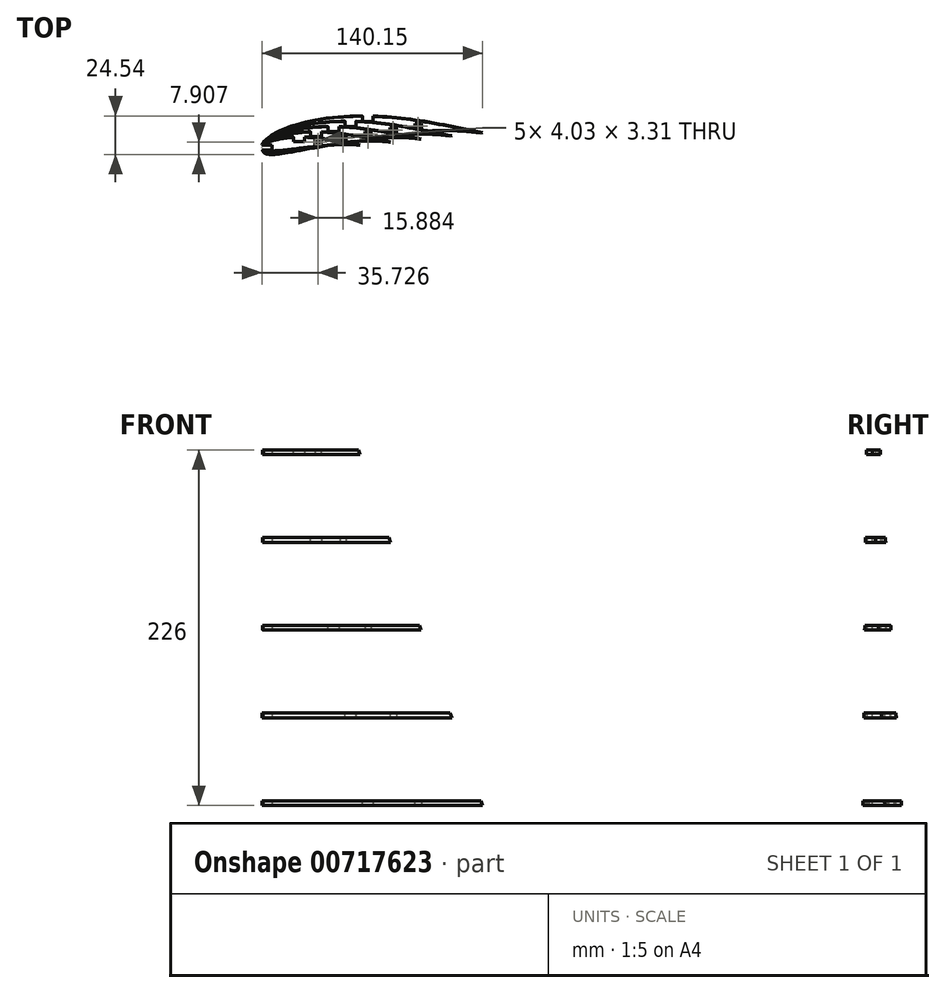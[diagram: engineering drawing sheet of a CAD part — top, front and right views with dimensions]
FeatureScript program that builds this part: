
annotation { "Feature Type Name" : "Feature", "Feature Type Description" : "" }
export const myFeature = defineFeature(function(context is Context, id is Id, definition is map)
    precondition{}
    {
        {
            var Q0;
            Q0=qCreatedBy(makeId("Top.planeOp"),FACE);
            var sketch = newSketch(context, id + "F0", { "sketchPlane" : qUnion([Q0])});
            skLineSegment(sketch, "E0", {"start": v(-0.42, 1.1) * mm, "end": v(1.04, 2.87) * mm});
            skLineSegment(sketch, "E1", {"start": v(1.04, 2.87) * mm, "end": v(2.54, 4.58) * mm});
            skLineSegment(sketch, "E2", {"start": v(2.54, 4.58) * mm, "end": v(4.15, 6.16) * mm});
            skLineSegment(sketch, "E3", {"start": v(4.15, 6.16) * mm, "end": v(4.64, 6.58) * mm});
            skLineSegment(sketch, "E4", {"start": v(4.64, 6.58) * mm, "end": v(5.9, 7.56) * mm});
            skLineSegment(sketch, "E5", {"start": v(5.9, 7.56) * mm, "end": v(7.8, 8.78) * mm});
            skLineSegment(sketch, "E6", {"start": v(7.8, 8.78) * mm, "end": v(9.8, 9.86) * mm});
            skLineSegment(sketch, "E7", {"start": v(9.8, 9.86) * mm, "end": v(11.89, 10.8) * mm});
            skLineSegment(sketch, "E8", {"start": v(11.89, 10.8) * mm, "end": v(15.88, 12.34) * mm});
            skLineSegment(sketch, "E9", {"start": v(15.88, 12.34) * mm, "end": v(18.36, 13.2) * mm});
            skLineSegment(sketch, "E10", {"start": v(18.36, 13.2) * mm, "end": v(22.7, 14.6) * mm});
            skLineSegment(sketch, "E11", {"start": v(22.7, 14.6) * mm, "end": v(27.05, 15.83) * mm});
            skLineSegment(sketch, "E12", {"start": v(27.05, 15.83) * mm, "end": v(32.46, 17.12) * mm});
            skLineSegment(sketch, "E13", {"start": v(32.46, 17.12) * mm, "end": v(35.87, 17.8) * mm});
            skLineSegment(sketch, "E14", {"start": v(35.87, 17.8) * mm, "end": v(40.34, 18.53) * mm});
            skLineSegment(sketch, "E15", {"start": v(40.34, 18.53) * mm, "end": v(44.84, 19.11) * mm});
            skLineSegment(sketch, "E16", {"start": v(44.84, 19.11) * mm, "end": v(49.37, 19.56) * mm});
            skLineSegment(sketch, "E17", {"start": v(49.37, 19.56) * mm, "end": v(52.55, 19.79) * mm});
            skLineSegment(sketch, "E18", {"start": v(52.55, 19.79) * mm, "end": v(58.48, 20.07) * mm});
            skLineSegment(sketch, "E19", {"start": v(58.48, 20.07) * mm, "end": v(63.03, 20.16) * mm});
            skLineSegment(sketch, "E20", {"start": v(63.03, 20.16) * mm, "end": v(67.58, 20.14) * mm});
            skLineSegment(sketch, "E21", {"start": v(67.58, 20.14) * mm, "end": v(72.1, 20.03) * mm});
            skLineSegment(sketch, "E22", {"start": v(72.1, 20.03) * mm, "end": v(74.6, 19.93) * mm});
            skLineSegment(sketch, "E23", {"start": v(74.6, 19.93) * mm, "end": v(81.02, 19.54) * mm});
            skLineSegment(sketch, "E24", {"start": v(81.02, 19.54) * mm, "end": v(85.48, 19.16) * mm});
            skLineSegment(sketch, "E25", {"start": v(85.48, 19.16) * mm, "end": v(90, 18.69) * mm});
            skLineSegment(sketch, "E26", {"start": v(90, 18.69) * mm, "end": v(96.67, 17.82) * mm});
            skLineSegment(sketch, "E27", {"start": v(96.67, 17.82) * mm, "end": v(99.3, 17.44) * mm});
            skLineSegment(sketch, "E28", {"start": v(99.3, 17.44) * mm, "end": v(104.05, 16.68) * mm});
            skLineSegment(sketch, "E29", {"start": v(104.05, 16.68) * mm, "end": v(108.68, 15.9) * mm});
            skLineSegment(sketch, "E30", {"start": v(108.68, 15.9) * mm, "end": v(110.9, 15.5) * mm});
            skLineSegment(sketch, "E31", {"start": v(110.9, 15.5) * mm, "end": v(113.04, 15.11) * mm});
            skLineSegment(sketch, "E32", {"start": v(113.04, 15.11) * mm, "end": v(115.07, 14.74) * mm});
            skLineSegment(sketch, "E33", {"start": v(115.07, 14.74) * mm, "end": v(116.62, 14.45) * mm});
            skLineSegment(sketch, "E34", {"start": v(116.62, 14.45) * mm, "end": v(120.51, 13.7) * mm});
            skLineSegment(sketch, "E35", {"start": v(120.51, 13.7) * mm, "end": v(122.38, 13.34) * mm});
            skLineSegment(sketch, "E36", {"start": v(122.38, 13.34) * mm, "end": v(123.38, 13.14) * mm});
            skLineSegment(sketch, "E37", {"start": v(123.38, 13.14) * mm, "end": v(124.45, 12.92) * mm});
            skLineSegment(sketch, "E38", {"start": v(124.45, 12.92) * mm, "end": v(125.6, 12.68) * mm});
            skLineSegment(sketch, "E39", {"start": v(125.6, 12.68) * mm, "end": v(126.84, 12.43) * mm});
            skLineSegment(sketch, "E40", {"start": v(126.84, 12.43) * mm, "end": v(128.18, 12.15) * mm});
            skLineSegment(sketch, "E41", {"start": v(128.18, 12.15) * mm, "end": v(129.65, 11.84) * mm});
            skLineSegment(sketch, "E42", {"start": v(129.65, 11.84) * mm, "end": v(131.93, 11.36) * mm});
            skLineSegment(sketch, "E43", {"start": v(131.93, 11.36) * mm, "end": v(133, 11.13) * mm});
            skLineSegment(sketch, "E44", {"start": v(133, 11.13) * mm, "end": v(134.82, 10.75) * mm});
            skLineSegment(sketch, "E45", {"start": v(134.82, 10.75) * mm, "end": v(136.58, 10.37) * mm});
            skLineSegment(sketch, "E46", {"start": v(136.58, 10.37) * mm, "end": v(137.4, 10.2) * mm});
            skLineSegment(sketch, "E47", {"start": v(137.4, 10.2) * mm, "end": v(138.16, 10.03) * mm});
            skLineSegment(sketch, "E48", {"start": v(138.16, 10.03) * mm, "end": v(138.83, 9.88) * mm});
            skLineSegment(sketch, "E49", {"start": v(138.83, 9.88) * mm, "end": v(139.4, 9.75) * mm});
            skLineSegment(sketch, "E50", {"start": v(139.4, 9.75) * mm, "end": v(139.86, 9.65) * mm});
            skLineSegment(sketch, "E51", {"start": v(139.86, 9.65) * mm, "end": v(140.2, 9.56) * mm});
            skLineSegment(sketch, "E52", {"start": v(140.2, 9.56) * mm, "end": v(140.38, 9.51) * mm});
            skLineSegment(sketch, "E53", {"start": v(140.38, 9.51) * mm, "end": v(140.4, 9.5) * mm});
            skLineSegment(sketch, "E54", {"start": v(140.4, 9.5) * mm, "end": v(140.24, 9.5) * mm});
            skLineSegment(sketch, "E55", {"start": v(140.24, 9.5) * mm, "end": v(140.08, 9.53) * mm});
            skLineSegment(sketch, "E56", {"start": v(140.08, 9.53) * mm, "end": v(139.36, 9.65) * mm});
            skLineSegment(sketch, "E57", {"start": v(139.36, 9.65) * mm, "end": v(138.4, 9.81) * mm});
            skLineSegment(sketch, "E58", {"start": v(138.4, 9.81) * mm, "end": v(136.21, 10.13) * mm});
            skLineSegment(sketch, "E59", {"start": v(136.21, 10.13) * mm, "end": v(133.85, 10.4) * mm});
            skLineSegment(sketch, "E60", {"start": v(133.85, 10.4) * mm, "end": v(131.61, 10.58) * mm});
            skLineSegment(sketch, "E61", {"start": v(131.61, 10.58) * mm, "end": v(126.03, 10.8) * mm});
            skLineSegment(sketch, "E62", {"start": v(126.03, 10.8) * mm, "end": v(122.98, 10.85) * mm});
            skLineSegment(sketch, "E63", {"start": v(122.98, 10.85) * mm, "end": v(118.52, 10.88) * mm});
            skLineSegment(sketch, "E64", {"start": v(118.52, 10.88) * mm, "end": v(113.95, 10.85) * mm});
            skLineSegment(sketch, "E65", {"start": v(113.95, 10.85) * mm, "end": v(109.34, 10.75) * mm});
            skLineSegment(sketch, "E66", {"start": v(109.34, 10.75) * mm, "end": v(103.97, 10.52) * mm});
            skLineSegment(sketch, "E67", {"start": v(103.97, 10.52) * mm, "end": v(100.13, 10.27) * mm});
            skLineSegment(sketch, "E68", {"start": v(100.13, 10.27) * mm, "end": v(95.58, 9.9) * mm});
            skLineSegment(sketch, "E69", {"start": v(95.58, 9.9) * mm, "end": v(91.07, 9.44) * mm});
            skLineSegment(sketch, "E70", {"start": v(91.07, 9.44) * mm, "end": v(86.57, 8.91) * mm});
            skLineSegment(sketch, "E71", {"start": v(86.57, 8.91) * mm, "end": v(76.85, 7.57) * mm});
            skLineSegment(sketch, "E72", {"start": v(76.85, 7.57) * mm, "end": v(68.73, 6.27) * mm});
            skLineSegment(sketch, "E73", {"start": v(68.73, 6.27) * mm, "end": v(59.8, 4.7) * mm});
            skLineSegment(sketch, "E74", {"start": v(59.8, 4.7) * mm, "end": v(49.88, 2.79) * mm});
            skLineSegment(sketch, "E75", {"start": v(49.88, 2.79) * mm, "end": v(41.82, 1.14) * mm});
            skLineSegment(sketch, "E76", {"start": v(41.82, 1.14) * mm, "end": v(37.34, 0.22) * mm});
            skLineSegment(sketch, "E77", {"start": v(37.34, 0.22) * mm, "end": v(32.9, -0.65) * mm});
            skLineSegment(sketch, "E78", {"start": v(32.9, -0.65) * mm, "end": v(26.98, -1.7) * mm});
            skLineSegment(sketch, "E79", {"start": v(26.98, -1.7) * mm, "end": v(24.24, -2.14) * mm});
            skLineSegment(sketch, "E80", {"start": v(24.24, -2.14) * mm, "end": v(19.94, -2.77) * mm});
            skLineSegment(sketch, "E81", {"start": v(19.94, -2.77) * mm, "end": v(17.73, -3.06) * mm});
            skLineSegment(sketch, "E82", {"start": v(17.73, -3.06) * mm, "end": v(15.45, -3.36) * mm});
            skLineSegment(sketch, "E83", {"start": v(15.45, -3.36) * mm, "end": v(13.08, -3.65) * mm});
            skLineSegment(sketch, "E84", {"start": v(13.08, -3.65) * mm, "end": v(10.68, -3.96) * mm});
            skLineSegment(sketch, "E85", {"start": v(10.68, -3.96) * mm, "end": v(8.03, -4.25) * mm});
            skLineSegment(sketch, "E86", {"start": v(8.03, -4.25) * mm, "end": v(6.75, -4.33) * mm});
            skLineSegment(sketch, "E87", {"start": v(6.75, -4.33) * mm, "end": v(5.52, -4.33) * mm});
            skLineSegment(sketch, "E88", {"start": v(5.52, -4.33) * mm, "end": v(4.36, -4.21) * mm});
            skLineSegment(sketch, "E89", {"start": v(4.36, -4.21) * mm, "end": v(3.3, -3.97) * mm});
            skLineSegment(sketch, "E90", {"start": v(3.3, -3.97) * mm, "end": v(2.34, -3.56) * mm});
            skLineSegment(sketch, "E91", {"start": v(2.34, -3.56) * mm, "end": v(1.92, -3.28) * mm});
            skLineSegment(sketch, "E92", {"start": v(1.92, -3.28) * mm, "end": v(1.4, -2.83) * mm});
            skLineSegment(sketch, "E93", {"start": v(1.4, -2.83) * mm, "end": v(1.19, -2.58) * mm});
            skLineSegment(sketch, "E94", {"start": v(1.19, -2.58) * mm, "end": v(0.89, -2.15) * mm});
            skLineSegment(sketch, "E95", {"start": v(0.89, -2.15) * mm, "end": v(0.38, -1.16) * mm});
            skLineSegment(sketch, "E96", {"start": v(0.38, -1.16) * mm, "end": v(-0.05, -0.06) * mm});
            skLineSegment(sketch, "E97", {"start": v(-0.05, -0.06) * mm, "end": v(-0.42, 1.1) * mm});
            skSolve(sketch);
        }
        {
            var Q0;
            Q0=qCreatedBy(makeId("Top.planeOp"),FACE);
            var sketch = newSketch(context, id + "F1", { "sketchPlane" : qUnion([Q0])});
            skPoint(sketch, "E98.0", {"position": v(0.94, -2.52) * mm});
            skPoint(sketch, "E98.1", {"position": v(0.64, -2.08) * mm});
            skPoint(sketch, "E98.2", {"position": v(0.13, -1.1) * mm});
            skPoint(sketch, "E98.3", {"position": v(0.8, 2.93) * mm});
            skPoint(sketch, "E98.5", {"position": v(40.1, 18.6) * mm});
            skPoint(sketch, "E98.6", {"position": v(85.24, 19.22) * mm});
            skPoint(sketch, "E98.7", {"position": v(140.15, 9.56) * mm});
            skPoint(sketch, "E98.8", {"position": v(125.78, 10.86) * mm});
            skPoint(sketch, "E98.9", {"position": v(99.89, 10.34) * mm});
            skPoint(sketch, "E98.10", {"position": v(49.63, 2.85) * mm});
            skPoint(sketch, "E98.11", {"position": v(12.84, -3.6) * mm});
            skPoint(sketch, "E98.12", {"position": v(2.1, -3.5) * mm});
            skPoint(sketch, "E98.13", {"position": v(5.28, -4.26) * mm});
            skFitSpline(sketch, "E99", {"points": [v(0.94, -2.52) * mm, v(2.1, -3.5) * mm, v(5.28, -4.26) * mm, v(12.84, -3.6) * mm, v(49.63, 2.85) * mm, v(99.89, 10.34) * mm, v(125.78, 10.86) * mm, v(140.15, 9.56) * mm], "startDerivative": vector(21.8, -23.84) * mm, "endDerivative": vector(100.11, -11.16) * mm});
            skPoint(sketch, "E100.0", {"position": v(11.64, 10.87) * mm});
            skFitSpline(sketch, "E101", {"points": [v(0.94, -2.52) * mm, v(0.64, -2.08) * mm, v(0.13, -1.1) * mm, v(0.8, 2.93) * mm, v(11.64, 10.87) * mm, v(40.1, 18.6) * mm, v(85.24, 19.22) * mm, v(140.15, 9.56) * mm], "startDerivative": vector(-10.5, 15.16) * mm, "endDerivative": vector(201.75, -43.18) * mm});
            skSolve(sketch);
        }
        {
            var Q0;
            Q0=qCreatedBy(makeId("Top.planeOp"),FACE);
            cPlane(context, id + "F2", {"entities" : qUnion([Q0]), "cplaneType" : CPlaneType.OFFSET, "offset" : 226 * mm, "width" : 150 * mm, "height" : 150 * mm});
        }
        {
            var Q0;
            Q0=qCreatedBy(id+"F2.planeOp",FACE);
            var sketch = newSketch(context, id + "F3", { "sketchPlane" : qUnion([Q0])});
            skPoint(sketch, "E102.0", {"position": v(0.64, -1.21) * mm});
            skPoint(sketch, "E102.1", {"position": v(0.07, -0.47) * mm});
            skPoint(sketch, "E102.2", {"position": v(0.27, 1.18) * mm});
            skPoint(sketch, "E102.3", {"position": v(2.53, 3.05) * mm});
            skPoint(sketch, "E102.4", {"position": v(15.91, 6.32) * mm});
            skPoint(sketch, "E102.5", {"position": v(32.82, 6.27) * mm});
            skPoint(sketch, "E102.6", {"position": v(61.27, 1.72) * mm});
            skPoint(sketch, "E102.7", {"position": v(55.5, 2.19) * mm});
            skPoint(sketch, "E102.8", {"position": v(33.37, 0.87) * mm});
            skPoint(sketch, "E102.9", {"position": v(18.25, -1.04) * mm});
            skPoint(sketch, "E102.10", {"position": v(10.5, -1.8) * mm});
            skPoint(sketch, "E102.11", {"position": v(1.43, -1.7) * mm});
            skPoint(sketch, "E102.12", {"position": v(2.88, -2) * mm});
            skFitSpline(sketch, "E103", {"points": [v(0.64, -1.21) * mm, v(0.07, -0.47) * mm, v(0.27, 1.18) * mm, v(2.53, 3.05) * mm, v(15.91, 6.32) * mm, v(32.82, 6.27) * mm, v(61.27, 1.72) * mm], "startDerivative": vector(-12.39, 11.02) * mm, "endDerivative": vector(97.43, -17.58) * mm});
            skFitSpline(sketch, "E104", {"points": [v(0.64, -1.21) * mm, v(1.43, -1.7) * mm, v(2.88, -2) * mm, v(10.5, -1.8) * mm, v(18.25, -1.04) * mm, v(33.37, 0.87) * mm, v(55.5, 2.19) * mm, v(61.27, 1.72) * mm], "startDerivative": vector(14.9, -10.52) * mm, "endDerivative": vector(36.47, -4.99) * mm});
            skSolve(sketch);
        }
        {
            var Q0;
            Q0=makeQuery(id+"F1.imprint","IMPRINT",FACE,{"disambiguationData":[TD([[makeQuery(id+"F1.imprint","IMPRINT",EDGE,{"derivedFrom":sQuery(id+"F1.wireOp",EDGE,"E99")}),1.0]])]});
            var Q1;
            Q1=makeQuery(id+"F3.imprint","IMPRINT",FACE,{"disambiguationData":[TD([[makeQuery(id+"F3.imprint","IMPRINT",EDGE,{"derivedFrom":sQuery(id+"F3.wireOp",EDGE,"E103")}),-1.0]])]});
            loft(context, id + "F4", {"sheetProfilesArray" : [{ "sheetProfileEntities" : qUnion([Q0]) }, { "sheetProfileEntities" : qUnion([Q1]) }]});
        }
        {
            var Q0;
            Q0=qCreatedBy(makeId("Front.planeOp"),FACE);
            var sketch = newSketch(context, id + "F5", { "sketchPlane" : qUnion([Q0])});
            skLineSegment(sketch, "E105", {"start": v(0, 0) * mm, "end": v(0, 3) * mm, "construction": true});
            skLineSegment(sketch, "E106.bottom", {"start": v(-6.3, 3) * mm, "end": v(175.34, 3) * mm});
            skLineSegment(sketch, "E106.top", {"start": v(-6.3, 55.75) * mm, "end": v(175.34, 55.75) * mm});
            skLineSegment(sketch, "E106.left", {"start": v(-6.3, 3) * mm, "end": v(-6.3, 55.75) * mm});
            skLineSegment(sketch, "E106.right", {"start": v(175.34, 3) * mm, "end": v(175.34, 55.75) * mm});
            skLineSegment(sketch, "E107.0.1.0", {"start": v(175.34, 58.75) * mm, "end": v(175.34, 111.5) * mm});
            skLineSegment(sketch, "E107.0.1.1", {"start": v(-6.3, 58.75) * mm, "end": v(-6.3, 111.5) * mm});
            skLineSegment(sketch, "E107.0.1.2", {"start": v(-6.3, 58.75) * mm, "end": v(175.34, 58.75) * mm});
            skLineSegment(sketch, "E107.0.1.3", {"start": v(-6.3, 111.5) * mm, "end": v(175.34, 111.5) * mm});
            skLineSegment(sketch, "E107.0.1.4", {"start": v(0, 55.75) * mm, "end": v(0, 58.75) * mm, "construction": true});
            skLineSegment(sketch, "E107.0.2.0", {"start": v(175.34, 114.5) * mm, "end": v(175.34, 167.25) * mm});
            skLineSegment(sketch, "E107.0.2.1", {"start": v(-6.3, 114.5) * mm, "end": v(-6.3, 167.25) * mm});
            skLineSegment(sketch, "E107.0.2.2", {"start": v(-6.3, 114.5) * mm, "end": v(175.34, 114.5) * mm});
            skLineSegment(sketch, "E107.0.2.3", {"start": v(-6.3, 167.25) * mm, "end": v(175.34, 167.25) * mm});
            skLineSegment(sketch, "E107.0.2.4", {"start": v(0, 111.5) * mm, "end": v(0, 114.5) * mm, "construction": true});
            skLineSegment(sketch, "E107.0.3.0", {"start": v(175.34, 170.25) * mm, "end": v(175.34, 223) * mm});
            skLineSegment(sketch, "E107.0.3.1", {"start": v(-6.3, 170.25) * mm, "end": v(-6.3, 223) * mm});
            skLineSegment(sketch, "E107.0.3.2", {"start": v(-6.3, 170.25) * mm, "end": v(175.34, 170.25) * mm});
            skLineSegment(sketch, "E107.0.3.3", {"start": v(-6.3, 223) * mm, "end": v(175.34, 223) * mm});
            skLineSegment(sketch, "E107.0.3.4", {"start": v(0, 167.25) * mm, "end": v(0, 170.25) * mm, "construction": true});
            skLineSegment(sketch, "E107.direction1", {"start": v(-6.3, 3) * mm, "end": v(18.7, 3) * mm, "construction": true});
            skLineSegment(sketch, "E107.direction2", {"start": v(-6.3, 3) * mm, "end": v(-6.3, 58.75) * mm, "construction": true});
            skSolve(sketch);
        }
        {
            var Q0;
            Q0=qSketchRegion(id+"F5",true);
            extrude(context, id + "F6", {"entities" : qUnion([Q0]), "operationType" : NewBodyOperationType.REMOVE, "oppositeDirection" : true, "depth" : 50 * mm, "offsetDistance" : 25 * mm, "hasSecondDirection" : true, "secondDirectionOppositeDirection" : false, "secondDirectionDepth" : 50 * mm});
        }
        {
            var Q0;
            Q0=qCreatedBy(makeId("Top.planeOp"),FACE);
            var sketch = newSketch(context, id + "F7", { "sketchPlane" : qUnion([Q0])});
            skLineSegment(sketch, "E108", {"start": v(0, 0) * mm, "end": v(6.35, 0) * mm, "construction": true});
            skLineSegment(sketch, "E109", {"start": v(6.35, 0) * mm, "end": v(6.35, 1.59) * mm});
            skLineSegment(sketch, "E110", {"start": v(6.35, 0) * mm, "end": v(6.35, -1.59) * mm});
            skLineSegment(sketch, "E111", {"start": v(6.35, -1.59) * mm, "end": v(0, -1.59) * mm});
            skLineSegment(sketch, "E112", {"start": v(0, -1.59) * mm, "end": v(0, 1.59) * mm});
            skLineSegment(sketch, "E113", {"start": v(0, 1.59) * mm, "end": v(6.35, 1.59) * mm});
            skSolve(sketch);
        }
        {
            var Q0;
            Q0=qSketchRegion(id+"F7",true);
            extrude(context, id + "F8", {"entities" : qUnion([Q0]), "operationType" : NewBodyOperationType.REMOVE, "depth" : 226 * mm, "offsetDistance" : 25 * mm});
        }
        {
            var Q0;
            Q0=makeQuery(id+"F4.opLoft","CAP_FACE",FACE,{"disambiguationData":[OSD([makeQuery(id+"F1.imprint","IMPRINT",FACE,{"disambiguationData":[TD([[makeQuery(id+"F1.imprint","IMPRINT",EDGE,{"derivedFrom":sQuery(id+"F1.wireOp",EDGE,"E99")}),1.0]])]})])],"isStart":true});
            var sketch = newSketch(context, id + "F9", { "sketchPlane" : qUnion([Q0])});
            skPoint(sketch, "E114.0", {"position": v(67.58, -20.14) * mm});
            skLineSegment(sketch, "E115", {"start": v(67.58, -20.14) * mm, "end": v(67.58, -16.97) * mm, "construction": true});
            skLineSegment(sketch, "E116", {"start": v(67.58, -16.97) * mm, "end": v(64.4, -16.97) * mm});
            skLineSegment(sketch, "E117", {"start": v(67.58, -16.97) * mm, "end": v(70.75, -16.97) * mm});
            skLineSegment(sketch, "E118", {"start": v(70.75, -16.97) * mm, "end": v(70.75, -20.47) * mm});
            skLineSegment(sketch, "E119", {"start": v(70.75, -20.47) * mm, "end": v(64.4, -20.47) * mm});
            skLineSegment(sketch, "E120", {"start": v(64.4, -20.47) * mm, "end": v(64.4, -16.97) * mm});
            skSolve(sketch);
        }
        {
            var Q0;
            Q0=makeQuery(id+"F3.imprint","IMPRINT",FACE,{"disambiguationData":[TD([[makeQuery(id+"F3.imprint","IMPRINT",EDGE,{"derivedFrom":sQuery(id+"F3.wireOp",EDGE,"E103")}),-1.0]])]});
            var sketch = newSketch(context, id + "F10", { "sketchPlane" : qUnion([Q0])});
            skFitSpline(sketch, "E121.0", {"points": [v(62.32, 1.83) * mm, v(59.72, 2.3) * mm, v(54.52, 3.24) * mm, v(46.72, 4.6) * mm, v(40.2, 5.61) * mm, v(34.96, 6.3) * mm, v(31.03, 6.7) * mm, v(27.08, 6.97) * mm, v(23.1, 7.03) * mm, v(19.18, 6.84) * mm, v(15.94, 6.47) * mm, v(13.37, 6.05) * mm, v(11.45, 5.7) * mm, v(9.54, 5.29) * mm, v(7.63, 4.82) * mm, v(5.74, 4.3) * mm, v(4.17, 3.78) * mm, v(2.93, 3.29) * mm, v(2.18, 2.93) * mm, v(1.6, 2.6) * mm, v(1.19, 2.31) * mm, v(0.81, 1.98) * mm, v(0.6, 1.73) * mm, v(0.5, 1.59) * mm]});
            skLineSegment(sketch, "E122", {"start": v(23.23, 7) * mm, "end": v(23.23, 3.82) * mm, "construction": true});
            skLineSegment(sketch, "E123", {"start": v(23.23, 3.82) * mm, "end": v(26.4, 3.82) * mm});
            skLineSegment(sketch, "E124", {"start": v(23.23, 3.82) * mm, "end": v(20.06, 3.82) * mm});
            skLineSegment(sketch, "E125", {"start": v(26.4, 3.82) * mm, "end": v(26.4, 7.32) * mm});
            skLineSegment(sketch, "E126", {"start": v(26.4, 7.32) * mm, "end": v(20.06, 7.32) * mm});
            skLineSegment(sketch, "E127", {"start": v(20.06, 7.32) * mm, "end": v(20.06, 3.82) * mm});
            skSolve(sketch);
        }
        {
            var Q0;
            Q0=makeQuery(id+"F1.imprint","IMPRINT",FACE,{"disambiguationData":[TD([[makeQuery(id+"F1.imprint","IMPRINT",EDGE,{"derivedFrom":sQuery(id+"F1.wireOp",EDGE,"E99")}),1.0]])]});
            var sketch = newSketch(context, id + "F11", { "sketchPlane" : qUnion([Q0])});
            skPoint(sketch, "E128.0", {"position": v(70.75, 16.97) * mm});
            skPoint(sketch, "E128.1", {"position": v(64.4, 16.97) * mm});
            skPoint(sketch, "E128.2", {"position": v(64.4, 20.47) * mm});
            skPoint(sketch, "E128.3", {"position": v(70.75, 20.47) * mm});
            skLineSegment(sketch, "E129", {"start": v(70.75, 20.47) * mm, "end": v(70.75, 16.97) * mm});
            skLineSegment(sketch, "E130", {"start": v(70.75, 16.97) * mm, "end": v(64.4, 16.97) * mm});
            skLineSegment(sketch, "E131", {"start": v(64.4, 16.97) * mm, "end": v(64.4, 20.47) * mm});
            skLineSegment(sketch, "E132", {"start": v(64.4, 20.47) * mm, "end": v(70.75, 20.47) * mm});
            skSolve(sketch);
        }
        {
            var Q0;
            Q0=makeQuery(id+"F3.imprint","IMPRINT",FACE,{"disambiguationData":[TD([[makeQuery(id+"F3.imprint","IMPRINT",EDGE,{"derivedFrom":sQuery(id+"F3.wireOp",EDGE,"E103")}),-1.0]])]});
            var sketch = newSketch(context, id + "F12", { "sketchPlane" : qUnion([Q0])});
            skPoint(sketch, "E133.0", {"position": v(20.06, 7.32) * mm});
            skPoint(sketch, "E133.1", {"position": v(20.06, 3.82) * mm});
            skPoint(sketch, "E133.2", {"position": v(26.4, 3.82) * mm});
            skPoint(sketch, "E133.3", {"position": v(26.4, 7.32) * mm});
            skLineSegment(sketch, "E134.bottom", {"start": v(20.06, 3.82) * mm, "end": v(26.4, 3.82) * mm});
            skLineSegment(sketch, "E134.top", {"start": v(20.06, 7.32) * mm, "end": v(26.4, 7.32) * mm});
            skLineSegment(sketch, "E134.left", {"start": v(20.06, 3.82) * mm, "end": v(20.06, 7.32) * mm});
            skLineSegment(sketch, "E134.right", {"start": v(26.4, 3.82) * mm, "end": v(26.4, 7.32) * mm});
            skSolve(sketch);
        }
        {
            var Q0;
            Q0=qSketchRegion(id+"F11",true);
            var Q1;
            Q1=qSketchRegion(id+"F12",true);
            loft(context, id + "F13", {"operationType" : NewBodyOperationType.REMOVE, "sheetProfilesArray" : [{ "sheetProfileEntities" : qUnion([Q0]) }, { "sheetProfileEntities" : qUnion([Q1]) }]});
        }
        {
            var Q0;
            Q0=makeQuery(id+"F1.imprint","IMPRINT",FACE,{"disambiguationData":[TD([[makeQuery(id+"F1.imprint","IMPRINT",EDGE,{"derivedFrom":sQuery(id+"F1.wireOp",EDGE,"E99")}),1.0]])]});
            var sketch = newSketch(context, id + "F14", { "sketchPlane" : qUnion([Q0])});
            skLineSegment(sketch, "E135.bottom", {"start": v(101.28, 15.47) * mm, "end": v(98.1, 15.47) * mm});
            skLineSegment(sketch, "E135.top", {"start": v(101.28, 12.3) * mm, "end": v(98.1, 12.3) * mm});
            skLineSegment(sketch, "E135.left", {"start": v(101.28, 15.47) * mm, "end": v(101.28, 12.3) * mm});
            skLineSegment(sketch, "E135.right", {"start": v(98.1, 15.47) * mm, "end": v(98.1, 12.3) * mm});
            skSolve(sketch);
        }
        {
            var Q0;
            Q0=makeQuery(id+"F3.imprint","IMPRINT",FACE,{"disambiguationData":[TD([[makeQuery(id+"F3.imprint","IMPRINT",EDGE,{"derivedFrom":sQuery(id+"F3.wireOp",EDGE,"E103")}),-1.0]])]});
            var sketch = newSketch(context, id + "F15", { "sketchPlane" : qUnion([Q0])});
            skLineSegment(sketch, "E136.bottom", {"start": v(33.71, 5.13) * mm, "end": v(36.89, 5.13) * mm});
            skLineSegment(sketch, "E136.top", {"start": v(33.71, 1.95) * mm, "end": v(36.89, 1.95) * mm});
            skLineSegment(sketch, "E136.left", {"start": v(33.71, 5.13) * mm, "end": v(33.71, 1.95) * mm});
            skLineSegment(sketch, "E136.right", {"start": v(36.89, 5.13) * mm, "end": v(36.89, 1.95) * mm});
            skSolve(sketch);
        }
        {
            var Q0;
            Q0=qSketchRegion(id+"F14",true);
            var Q1;
            Q1=qSketchRegion(id+"F15",true);
            loft(context, id + "F16", {"operationType" : NewBodyOperationType.REMOVE, "sheetProfilesArray" : [{ "sheetProfileEntities" : qUnion([Q0]) }, { "sheetProfileEntities" : qUnion([Q1]) }]});
        }
        {
            var Q0;
            Q0=makeQuery(id+"F4.opLoft","CAP_FACE",FACE,{"disambiguationData":[OSD([makeQuery(id+"F3.imprint","IMPRINT",FACE,{"disambiguationData":[TD([[makeQuery(id+"F3.imprint","IMPRINT",EDGE,{"derivedFrom":sQuery(id+"F3.wireOp",EDGE,"E103")}),-1.0]])]})])],"isStart":true});
            var sketch = newSketch(context, id + "F17", { "sketchPlane" : qUnion([Q0])});
            skLineSegment(sketch, "E137.0", {"start": v(20.06, 6.72) * mm, "end": v(20.06, 3.82) * mm});
            skLineSegment(sketch, "E137.1", {"start": v(20.06, 3.82) * mm, "end": v(26.4, 3.82) * mm});
            skLineSegment(sketch, "E137.2", {"start": v(33.71, 5.13) * mm, "end": v(33.71, 1.95) * mm});
            skLineSegment(sketch, "E137.3", {"start": v(36.89, 1.95) * mm, "end": v(36.89, 5.13) * mm});
            skLineSegment(sketch, "E138", {"start": v(26.4, 3.82) * mm, "end": v(26.4, 7.57) * mm});
            skLineSegment(sketch, "E139", {"start": v(26.4, 7.57) * mm, "end": v(20.06, 7.57) * mm});
            skLineSegment(sketch, "E140", {"start": v(20.06, 7.57) * mm, "end": v(20.06, 6.72) * mm});
            skLineSegment(sketch, "E141", {"start": v(33.71, 5.13) * mm, "end": v(36.89, 5.13) * mm});
            skLineSegment(sketch, "E142", {"start": v(36.89, 1.95) * mm, "end": v(33.71, 1.95) * mm});
            skSolve(sketch);
        }
        {
            var Q0;
            Q0=qSketchRegion(id+"F17",true);
            extrude(context, id + "F18", {"entities" : qUnion([Q0]), "operationType" : NewBodyOperationType.REMOVE, "oppositeDirection" : true, "depth" : 25 * mm, "offsetDistance" : 25 * mm});
        }
        {
            var Q0;
            Q0=makeQuery(id+"F6.boolean.opBoolean","COPY",FACE,{"derivedFrom":makeQuery(id+"F6.opExtrude","SWEPT_FACE",FACE,{"disambiguationData":[OSD([sQuery(id+"F5.wireOp",EDGE,"E107.0.3.2")])]})});
            var sketch = newSketch(context, id + "F19", { "sketchPlane" : qUnion([Q0])});
            skLineSegment(sketch, "E143.0", {"start": v(31, 7.06) * mm, "end": v(31, 10.06) * mm});
            skLineSegment(sketch, "E143.1", {"start": v(37.35, 7.06) * mm, "end": v(31, 7.06) * mm});
            skLineSegment(sketch, "E143.2", {"start": v(49.6, 4.5) * mm, "end": v(49.6, 7.68) * mm});
            skLineSegment(sketch, "E143.3", {"start": v(52.77, 7.68) * mm, "end": v(52.77, 4.5) * mm});
            skLineSegment(sketch, "E144", {"start": v(37.35, 7.06) * mm, "end": v(37.35, 11.42) * mm});
            skLineSegment(sketch, "E145", {"start": v(37.35, 11.42) * mm, "end": v(31, 11.42) * mm});
            skLineSegment(sketch, "E146", {"start": v(31, 11.42) * mm, "end": v(31, 10.06) * mm});
            skLineSegment(sketch, "E147", {"start": v(49.6, 7.68) * mm, "end": v(52.77, 7.68) * mm});
            skLineSegment(sketch, "E148", {"start": v(52.77, 4.5) * mm, "end": v(49.6, 4.5) * mm});
            skSolve(sketch);
        }
        {
            var Q0;
            Q0=qSketchRegion(id+"F19",true);
            extrude(context, id + "F20", {"entities" : qUnion([Q0]), "operationType" : NewBodyOperationType.REMOVE, "oppositeDirection" : true, "depth" : 25 * mm, "offsetDistance" : 25 * mm});
        }
        {
            var Q0;
            Q0=makeQuery(id+"F6.boolean.opBoolean","COPY",FACE,{"derivedFrom":makeQuery(id+"F6.opExtrude","SWEPT_FACE",FACE,{"disambiguationData":[OSD([sQuery(id+"F5.wireOp",EDGE,"E107.0.2.2")])]})});
            var sketch = newSketch(context, id + "F21", { "sketchPlane" : qUnion([Q0])});
            skLineSegment(sketch, "E149.0", {"start": v(41.93, 10.3) * mm, "end": v(41.93, 13.4) * mm});
            skLineSegment(sketch, "E149.1", {"start": v(48.28, 10.3) * mm, "end": v(41.93, 10.3) * mm});
            skLineSegment(sketch, "E149.2", {"start": v(65.48, 7.05) * mm, "end": v(65.48, 10.23) * mm});
            skLineSegment(sketch, "E149.3", {"start": v(68.65, 10.23) * mm, "end": v(68.65, 7.05) * mm});
            skLineSegment(sketch, "E150", {"start": v(48.28, 10.3) * mm, "end": v(48.28, 15.15) * mm});
            skLineSegment(sketch, "E151", {"start": v(48.28, 15.15) * mm, "end": v(41.93, 15.15) * mm});
            skLineSegment(sketch, "E152", {"start": v(41.93, 15.15) * mm, "end": v(41.93, 13.4) * mm});
            skLineSegment(sketch, "E153", {"start": v(65.48, 10.23) * mm, "end": v(68.65, 10.23) * mm});
            skLineSegment(sketch, "E154", {"start": v(68.65, 7.05) * mm, "end": v(65.48, 7.05) * mm});
            skSolve(sketch);
        }
        {
            var Q0;
            Q0=qSketchRegion(id+"F21",true);
            extrude(context, id + "F22", {"entities" : qUnion([Q0]), "operationType" : NewBodyOperationType.REMOVE, "oppositeDirection" : true, "depth" : 25 * mm, "offsetDistance" : 25 * mm});
        }
        {
            var Q0;
            Q0=makeQuery(id+"F6.boolean.opBoolean","COPY",FACE,{"derivedFrom":makeQuery(id+"F6.opExtrude","SWEPT_FACE",FACE,{"disambiguationData":[OSD([sQuery(id+"F5.wireOp",EDGE,"E107.0.1.2")])]})});
            var sketch = newSketch(context, id + "F23", { "sketchPlane" : qUnion([Q0])});
            skLineSegment(sketch, "E155.0", {"start": v(52.87, 13.55) * mm, "end": v(52.87, 16.72) * mm});
            skLineSegment(sketch, "E155.1", {"start": v(59.22, 13.55) * mm, "end": v(52.87, 13.55) * mm});
            skLineSegment(sketch, "E155.2", {"start": v(81.36, 9.6) * mm, "end": v(81.36, 12.78) * mm});
            skLineSegment(sketch, "E155.3", {"start": v(84.54, 12.78) * mm, "end": v(84.54, 9.6) * mm});
            skLineSegment(sketch, "E156", {"start": v(59.22, 13.55) * mm, "end": v(59.22, 18.7) * mm});
            skLineSegment(sketch, "E157", {"start": v(59.22, 18.7) * mm, "end": v(52.87, 18.7) * mm});
            skLineSegment(sketch, "E158", {"start": v(52.87, 18.7) * mm, "end": v(52.87, 16.72) * mm});
            skLineSegment(sketch, "E159", {"start": v(81.36, 12.78) * mm, "end": v(84.54, 12.78) * mm});
            skLineSegment(sketch, "E160", {"start": v(81.36, 9.6) * mm, "end": v(84.54, 9.6) * mm});
            skSolve(sketch);
        }
        {
            var Q0;
            Q0=qSketchRegion(id+"F23",true);
            extrude(context, id + "F24", {"entities" : qUnion([Q0]), "operationType" : NewBodyOperationType.REMOVE, "oppositeDirection" : true, "depth" : 25 * mm, "offsetDistance" : 25 * mm});
        }
        {
            var Q0;
            Q0=makeQuery(id+"F6.boolean.opBoolean","COPY",FACE,{"derivedFrom":makeQuery(id+"F6.opExtrude","SWEPT_FACE",FACE,{"disambiguationData":[OSD([sQuery(id+"F5.wireOp",EDGE,"E106.bottom")])]})});
            var sketch = newSketch(context, id + "F25", { "sketchPlane" : qUnion([Q0])});
            skLineSegment(sketch, "E161.0", {"start": v(63.81, 16.8) * mm, "end": v(63.81, 20.06) * mm});
            skLineSegment(sketch, "E161.1", {"start": v(70.16, 16.8) * mm, "end": v(63.81, 16.8) * mm});
            skLineSegment(sketch, "E161.2", {"start": v(97.25, 12.16) * mm, "end": v(97.25, 15.33) * mm});
            skLineSegment(sketch, "E161.3", {"start": v(100.42, 15.33) * mm, "end": v(100.42, 12.16) * mm});
            skLineSegment(sketch, "E162", {"start": v(70.16, 16.8) * mm, "end": v(70.16, 21.68) * mm});
            skLineSegment(sketch, "E163", {"start": v(70.16, 21.68) * mm, "end": v(63.81, 21.68) * mm});
            skLineSegment(sketch, "E164", {"start": v(63.81, 21.68) * mm, "end": v(63.81, 20.06) * mm});
            skLineSegment(sketch, "E165", {"start": v(97.25, 15.33) * mm, "end": v(100.42, 15.33) * mm});
            skLineSegment(sketch, "E166", {"start": v(100.42, 12.16) * mm, "end": v(97.25, 12.16) * mm});
            skSolve(sketch);
        }
        {
            var Q0;
            Q0=qSketchRegion(id+"F25",true);
            extrude(context, id + "F26", {"entities" : qUnion([Q0]), "operationType" : NewBodyOperationType.REMOVE, "oppositeDirection" : true, "depth" : 25 * mm, "offsetDistance" : 25 * mm});
        }
        {
            var Q0;
            Q0=makeQuery(id+"F4.opLoft","CAP_FACE",FACE,{"disambiguationData":[OSD([makeQuery(id+"F1.imprint","IMPRINT",FACE,{"disambiguationData":[TD([[makeQuery(id+"F1.imprint","IMPRINT",EDGE,{"derivedFrom":sQuery(id+"F1.wireOp",EDGE,"E99")}),1.0]])]})])],"isStart":true});
            var sketch = newSketch(context, id + "F27", { "sketchPlane" : qUnion([Q0])});
            skLineSegment(sketch, "E167.0", {"start": v(70.75, -16.97) * mm, "end": v(70.75, -20.15) * mm});
            skLineSegment(sketch, "E167.1", {"start": v(70.16, -16.8) * mm, "end": v(63.81, -16.8) * mm});
            skLineSegment(sketch, "E168", {"start": v(70.16, -16.8) * mm, "end": v(70.75, -16.8) * mm});
            skLineSegment(sketch, "E169", {"start": v(70.75, -16.8) * mm, "end": v(70.75, -16.97) * mm});
            skLineSegment(sketch, "E170", {"start": v(63.81, -16.8) * mm, "end": v(63.81, -21.12) * mm});
            skLineSegment(sketch, "E171", {"start": v(63.81, -21.12) * mm, "end": v(70.75, -21.12) * mm});
            skLineSegment(sketch, "E172", {"start": v(70.75, -21.12) * mm, "end": v(70.75, -20.15) * mm});
            skLineSegment(sketch, "E173.0", {"start": v(97.25, -12.16) * mm, "end": v(97.25, -15.33) * mm});
            skLineSegment(sketch, "E173.1", {"start": v(101.28, -15.47) * mm, "end": v(98.1, -15.47) * mm});
            skLineSegment(sketch, "E174", {"start": v(97.25, -15.33) * mm, "end": v(97.25, -15.47) * mm});
            skLineSegment(sketch, "E175", {"start": v(97.25, -15.47) * mm, "end": v(98.1, -15.47) * mm});
            skLineSegment(sketch, "E176", {"start": v(101.28, -15.47) * mm, "end": v(101.28, -12.16) * mm});
            skPoint(sketch, "E176.endSnap0", {"position": v(98.83, -12.16) * mm});
            skLineSegment(sketch, "E177", {"start": v(101.28, -12.16) * mm, "end": v(97.25, -12.16) * mm});
            skSolve(sketch);
        }
        {
            var Q0;
            Q0=qSketchRegion(id+"F27",true);
            extrude(context, id + "F28", {"entities" : qUnion([Q0]), "operationType" : NewBodyOperationType.REMOVE, "oppositeDirection" : true, "depth" : 25 * mm, "offsetDistance" : 25 * mm});
        }
        {
            var Q0;
            Q0=makeQuery(id+"F6.boolean.opBoolean","COPY",FACE,{"derivedFrom":makeQuery(id+"F6.opExtrude","SWEPT_FACE",FACE,{"disambiguationData":[OSD([sQuery(id+"F5.wireOp",EDGE,"E106.top")])]})});
            var sketch = newSketch(context, id + "F29", { "sketchPlane" : qUnion([Q0])});
            skLineSegment(sketch, "E178.0", {"start": v(52.87, -13.55) * mm, "end": v(59.22, -13.55) * mm});
            skLineSegment(sketch, "E178.1", {"start": v(59.81, -16.82) * mm, "end": v(59.81, -13.72) * mm});
            skLineSegment(sketch, "E178.2", {"start": v(81.36, -12.78) * mm, "end": v(81.36, -9.6) * mm});
            skLineSegment(sketch, "E178.3", {"start": v(82.22, -12.92) * mm, "end": v(85.4, -12.92) * mm});
            skLineSegment(sketch, "E179", {"start": v(59.22, -13.55) * mm, "end": v(59.81, -13.55) * mm});
            skLineSegment(sketch, "E180", {"start": v(59.81, -13.55) * mm, "end": v(59.81, -13.72) * mm});
            skLineSegment(sketch, "E181", {"start": v(59.81, -16.82) * mm, "end": v(59.81, -17.44) * mm});
            skLineSegment(sketch, "E182", {"start": v(59.81, -17.44) * mm, "end": v(52.87, -17.44) * mm});
            skLineSegment(sketch, "E183", {"start": v(52.87, -17.44) * mm, "end": v(52.87, -13.55) * mm});
            skLineSegment(sketch, "E184", {"start": v(81.36, -12.78) * mm, "end": v(81.36, -12.92) * mm});
            skLineSegment(sketch, "E185", {"start": v(81.36, -12.92) * mm, "end": v(82.22, -12.92) * mm});
            skLineSegment(sketch, "E186", {"start": v(85.4, -12.92) * mm, "end": v(85.4, -9.6) * mm});
            skLineSegment(sketch, "E187", {"start": v(85.4, -9.6) * mm, "end": v(81.36, -9.6) * mm});
            skSolve(sketch);
        }
        {
            var Q0;
            Q0=qSketchRegion(id+"F29",true);
            extrude(context, id + "F30", {"entities" : qUnion([Q0]), "operationType" : NewBodyOperationType.REMOVE, "oppositeDirection" : true, "depth" : 25 * mm, "offsetDistance" : 25 * mm});
        }
        {
            var Q0;
            Q0=makeQuery(id+"F6.boolean.opBoolean","COPY",FACE,{"derivedFrom":makeQuery(id+"F6.opExtrude","SWEPT_FACE",FACE,{"disambiguationData":[OSD([sQuery(id+"F5.wireOp",EDGE,"E107.0.1.3")])]})});
            var sketch = newSketch(context, id + "F31", { "sketchPlane" : qUnion([Q0])});
            skLineSegment(sketch, "E188.0", {"start": v(41.93, -10.3) * mm, "end": v(48.28, -10.3) * mm});
            skLineSegment(sketch, "E188.1", {"start": v(48.87, -13.5) * mm, "end": v(48.87, -10.48) * mm});
            skLineSegment(sketch, "E188.2", {"start": v(65.48, -10.23) * mm, "end": v(65.48, -7.05) * mm});
            skLineSegment(sketch, "E188.3", {"start": v(66.33, -10.37) * mm, "end": v(69.5, -10.37) * mm});
            skLineSegment(sketch, "E189", {"start": v(48.87, -10.48) * mm, "end": v(48.87, -10.3) * mm});
            skLineSegment(sketch, "E190", {"start": v(48.87, -10.3) * mm, "end": v(48.28, -10.3) * mm});
            skLineSegment(sketch, "E191", {"start": v(41.93, -10.3) * mm, "end": v(41.93, -14.16) * mm});
            skLineSegment(sketch, "E192", {"start": v(41.93, -14.16) * mm, "end": v(48.87, -14.16) * mm});
            skLineSegment(sketch, "E193", {"start": v(48.87, -14.16) * mm, "end": v(48.87, -13.5) * mm});
            skLineSegment(sketch, "E194", {"start": v(65.48, -10.23) * mm, "end": v(65.48, -10.37) * mm});
            skLineSegment(sketch, "E195", {"start": v(65.48, -10.37) * mm, "end": v(66.33, -10.37) * mm});
            skLineSegment(sketch, "E196", {"start": v(69.5, -10.37) * mm, "end": v(69.5, -7.05) * mm});
            skPoint(sketch, "E196.endSnap0", {"position": v(67.07, -7.05) * mm});
            skLineSegment(sketch, "E197", {"start": v(69.5, -7.05) * mm, "end": v(65.48, -7.05) * mm});
            skSolve(sketch);
        }
        {
            var Q0;
            Q0=qSketchRegion(id+"F31",true);
            extrude(context, id + "F32", {"entities" : qUnion([Q0]), "operationType" : NewBodyOperationType.REMOVE, "oppositeDirection" : true, "depth" : 25 * mm, "offsetDistance" : 25 * mm});
        }
        {
            var Q0;
            Q0=makeQuery(id+"F6.boolean.opBoolean","COPY",FACE,{"derivedFrom":makeQuery(id+"F6.opExtrude","SWEPT_FACE",FACE,{"disambiguationData":[OSD([sQuery(id+"F5.wireOp",EDGE,"E107.0.2.3")])]})});
            var sketch = newSketch(context, id + "F33", { "sketchPlane" : qUnion([Q0])});
            skLineSegment(sketch, "E198.0", {"start": v(31, -7.06) * mm, "end": v(37.35, -7.06) * mm});
            skLineSegment(sketch, "E198.1", {"start": v(37.93, -10.2) * mm, "end": v(37.93, -7.24) * mm});
            skLineSegment(sketch, "E198.2", {"start": v(49.6, -7.68) * mm, "end": v(49.6, -4.5) * mm});
            skLineSegment(sketch, "E198.3", {"start": v(50.45, -7.81) * mm, "end": v(53.62, -7.81) * mm});
            skLineSegment(sketch, "E199", {"start": v(37.35, -7.06) * mm, "end": v(37.93, -7.06) * mm});
            skLineSegment(sketch, "E200", {"start": v(37.93, -7.06) * mm, "end": v(37.93, -7.24) * mm});
            skLineSegment(sketch, "E201", {"start": v(31, -7.06) * mm, "end": v(31, -11.38) * mm});
            skLineSegment(sketch, "E202", {"start": v(31, -11.38) * mm, "end": v(37.93, -11.38) * mm});
            skLineSegment(sketch, "E203", {"start": v(37.93, -11.38) * mm, "end": v(37.93, -10.2) * mm});
            skLineSegment(sketch, "E204", {"start": v(49.6, -7.68) * mm, "end": v(49.6, -7.81) * mm});
            skLineSegment(sketch, "E205", {"start": v(49.6, -7.81) * mm, "end": v(50.45, -7.81) * mm});
            skLineSegment(sketch, "E206", {"start": v(53.62, -7.81) * mm, "end": v(53.62, -4.5) * mm});
            skLineSegment(sketch, "E207", {"start": v(53.62, -4.5) * mm, "end": v(49.6, -4.5) * mm});
            skSolve(sketch);
        }
        {
            var Q0;
            Q0=qSketchRegion(id+"F33",true);
            extrude(context, id + "F34", {"entities" : qUnion([Q0]), "operationType" : NewBodyOperationType.REMOVE, "oppositeDirection" : true, "depth" : 25 * mm, "offsetDistance" : 25 * mm});
        }
        {
            var Q0;
            Q0=makeQuery(id+"F6.boolean.opBoolean","COPY",FACE,{"derivedFrom":makeQuery(id+"F6.opExtrude","SWEPT_FACE",FACE,{"disambiguationData":[OSD([sQuery(id+"F5.wireOp",EDGE,"E107.0.3.3")])]})});
            var sketch = newSketch(context, id + "F35", { "sketchPlane" : qUnion([Q0])});
            skLineSegment(sketch, "E208.0", {"start": v(26.4, -3.82) * mm, "end": v(20.06, -3.82) * mm});
            skLineSegment(sketch, "E208.1", {"start": v(27, -6.94) * mm, "end": v(27, -4) * mm});
            skLineSegment(sketch, "E208.2", {"start": v(33.71, -1.95) * mm, "end": v(33.71, -5.13) * mm});
            skLineSegment(sketch, "E208.3", {"start": v(34.57, -5.26) * mm, "end": v(37.74, -5.26) * mm});
            skLineSegment(sketch, "E209", {"start": v(26.4, -3.82) * mm, "end": v(27, -3.82) * mm});
            skLineSegment(sketch, "E210", {"start": v(27, -3.82) * mm, "end": v(27, -4) * mm});
            skLineSegment(sketch, "E211", {"start": v(20.06, -3.82) * mm, "end": v(20.06, -7.33) * mm});
            skLineSegment(sketch, "E212", {"start": v(20.06, -7.33) * mm, "end": v(27, -7.33) * mm});
            skLineSegment(sketch, "E213", {"start": v(27, -7.33) * mm, "end": v(27, -6.94) * mm});
            skLineSegment(sketch, "E214", {"start": v(33.71, -5.13) * mm, "end": v(33.71, -5.26) * mm});
            skLineSegment(sketch, "E215", {"start": v(33.71, -5.26) * mm, "end": v(34.57, -5.26) * mm});
            skLineSegment(sketch, "E216", {"start": v(37.74, -5.26) * mm, "end": v(37.74, -1.95) * mm});
            skPoint(sketch, "E216.endSnap0", {"position": v(35.3, -1.95) * mm});
            skLineSegment(sketch, "E217", {"start": v(37.74, -1.95) * mm, "end": v(33.71, -1.95) * mm});
            skSolve(sketch);
        }
        {
            var Q0;
            Q0=qSketchRegion(id+"F35",true);
            extrude(context, id + "F36", {"entities" : qUnion([Q0]), "operationType" : NewBodyOperationType.REMOVE, "oppositeDirection" : true, "depth" : 25 * mm, "offsetDistance" : 25 * mm});
        }
    });
